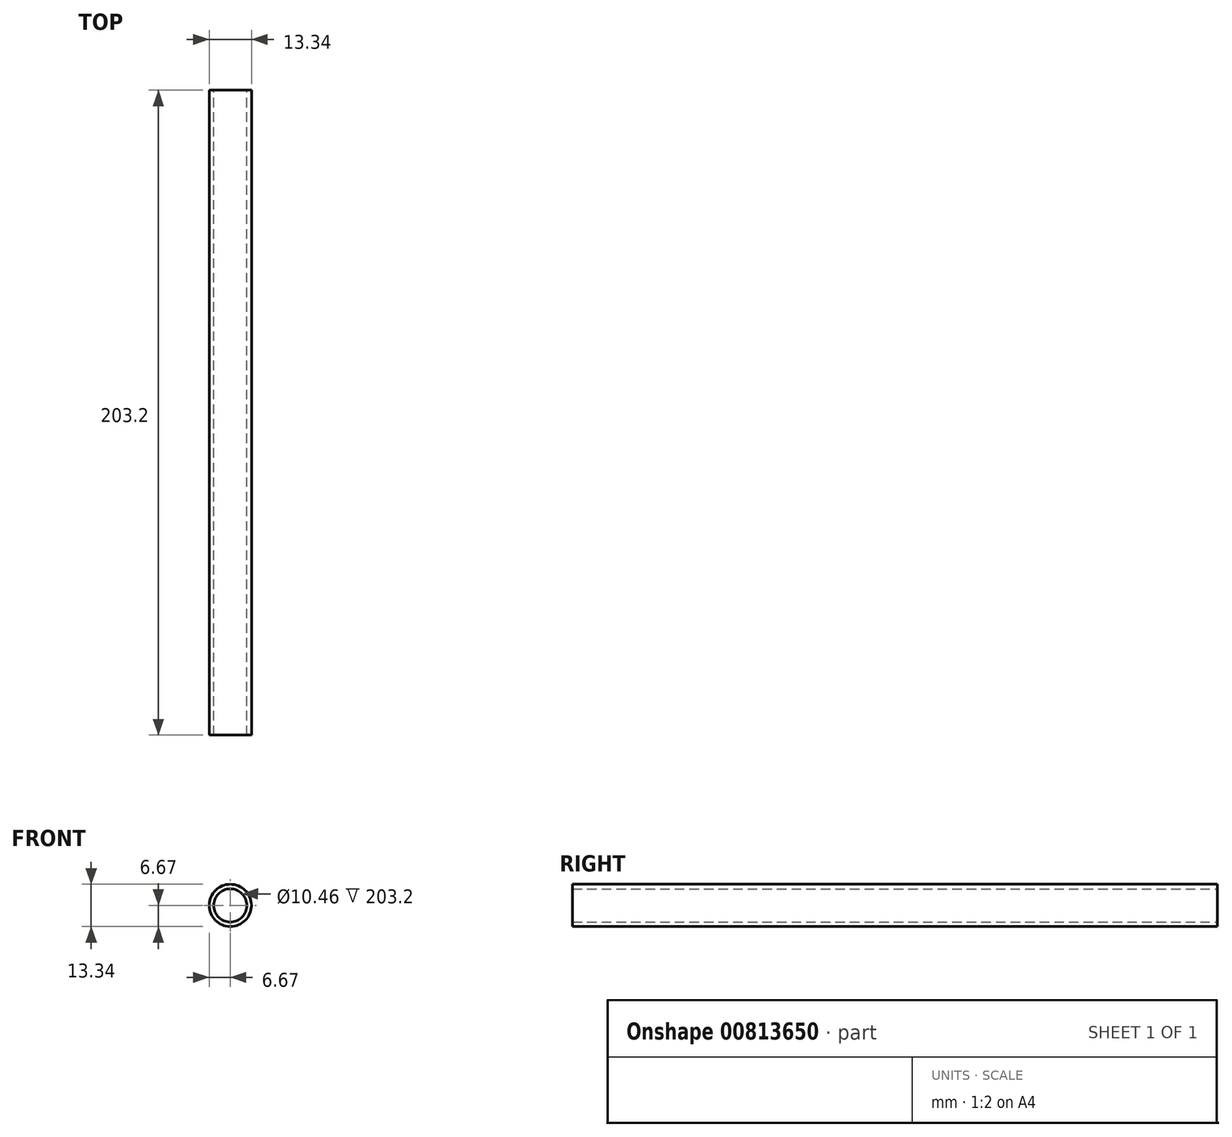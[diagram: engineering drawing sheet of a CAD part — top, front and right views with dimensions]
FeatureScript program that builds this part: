
annotation { "Feature Type Name" : "Feature", "Feature Type Description" : "" }
export const myFeature = defineFeature(function(context is Context, id is Id, definition is map)
    precondition{}
    {
        {
            var Q0;
            Q0=qCreatedBy(makeId("Front.planeOp"),FACE);
            var sketch = newSketch(context, id + "F0", { "sketchPlane" : qUnion([Q0])});
            skCircle(sketch, "E0", {"center": v(0, 0) * mm, "radius": 6.67 * mm});
            skCircle(sketch, "E1", {"center": v(0, 0) * mm, "radius": 5.23 * mm});
            skSolve(sketch);
        }
        {
            var Q0;
            Q0=qSketchRegion(id+"F0",true);
            extrude(context, id + "F1", {"entities" : qUnion([Q0]), "endBound" : BoundingType.SYMMETRIC, "depth" : 203.2 * mm, "offsetDistance" : 25.4 * mm});
        }
    });
